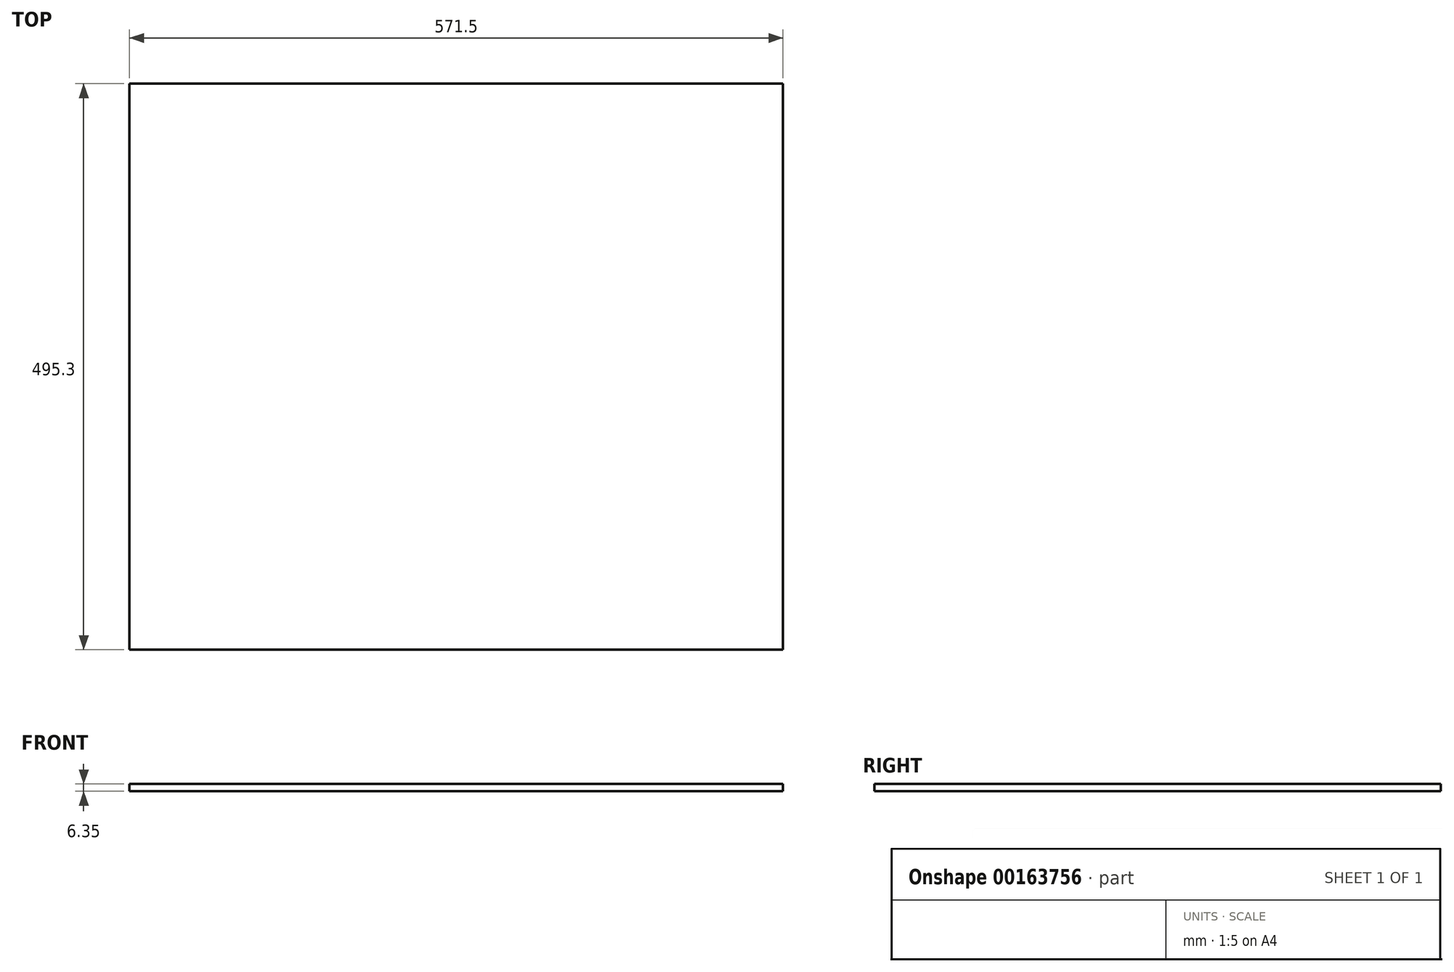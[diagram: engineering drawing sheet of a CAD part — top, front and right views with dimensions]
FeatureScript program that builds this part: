
annotation { "Feature Type Name" : "Feature", "Feature Type Description" : "" }
export const myFeature = defineFeature(function(context is Context, id is Id, definition is map)
    precondition{}
    {
        {
            var Q0;
            Q0=qCreatedBy(makeId("Top.planeOp"),FACE);
            var sketch = newSketch(context, id + "F0", { "sketchPlane" : qUnion([Q0])});
            skLineSegment(sketch, "E0.bottom", {"start": v(285.75, 247.65) * mm, "end": v(-285.75, 247.65) * mm});
            skLineSegment(sketch, "E0.top", {"start": v(285.75, -247.65) * mm, "end": v(-285.75, -247.65) * mm});
            skLineSegment(sketch, "E0.left", {"start": v(285.75, 247.65) * mm, "end": v(285.75, -247.65) * mm});
            skLineSegment(sketch, "E0.right", {"start": v(-285.75, 247.65) * mm, "end": v(-285.75, -247.65) * mm});
            skPoint(sketch, "E0.middle", {"position": v(0, 0) * mm});
            skSolve(sketch);
        }
        {
            var Q0;
            Q0=qSketchRegion(id+"F0",true);
            extrude(context, id + "F1", {"entities" : qUnion([Q0]), "depth" : 6.35 * mm, "offsetDistance" : 25.4 * mm});
        }
    });
